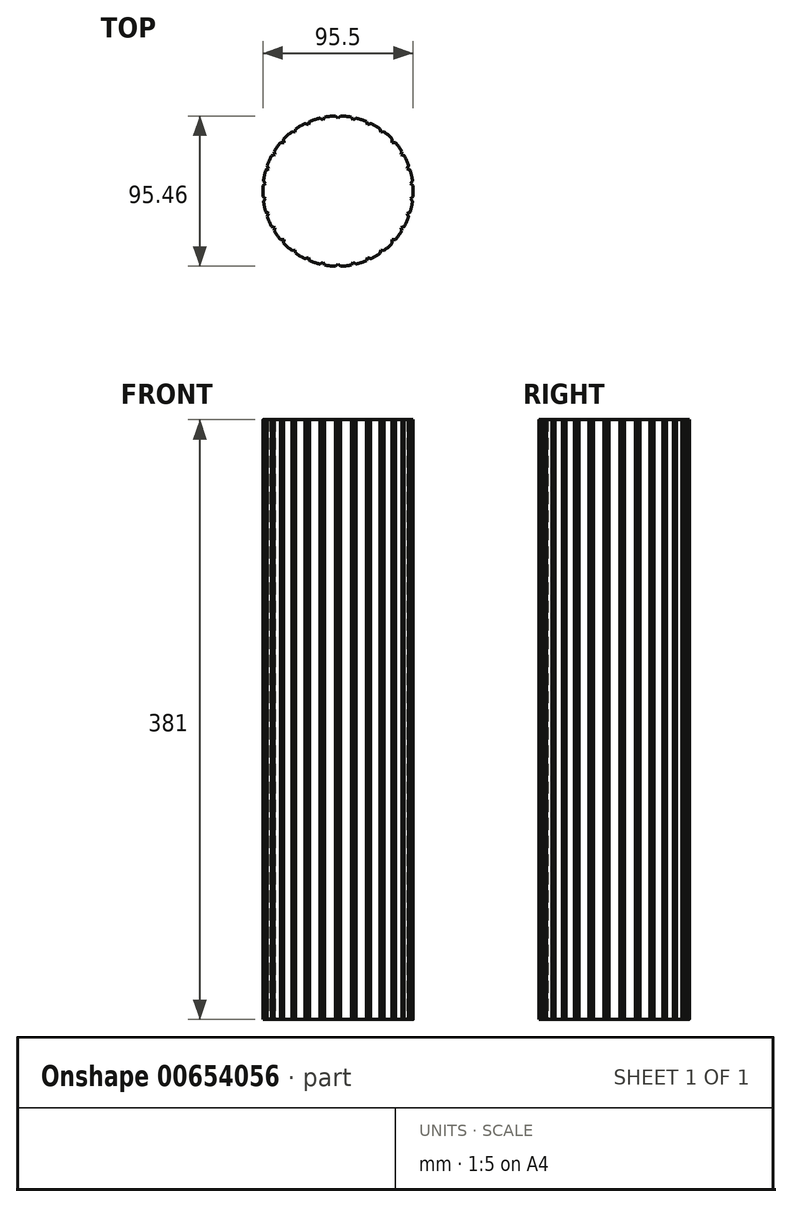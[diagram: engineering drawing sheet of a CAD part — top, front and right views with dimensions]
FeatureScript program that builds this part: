
annotation { "Feature Type Name" : "Feature", "Feature Type Description" : "" }
export const myFeature = defineFeature(function(context is Context, id is Id, definition is map)
    precondition{}
    {
        {
            var Q0;
            Q0=qCreatedBy(makeId("Top.planeOp"),FACE);
            var sketch = newSketch(context, id + "F0", { "sketchPlane" : qUnion([Q0])});
            skArc(sketch, "E0", {"start": v(1.5, -47.73) * mm, "mid": v(28.07, 38.63) * mm, "end": v(-45.86, -13.32) * mm});
            skLineSegment(sketch, "E1", {"start": v(1.5, -47.73) * mm, "end": v(0, -46.23) * mm});
            skLineSegment(sketch, "E2", {"start": v(0, -46.23) * mm, "end": v(-1.5, -47.73) * mm});
            skLineSegment(sketch, "E3.1.0", {"start": v(40.58, 25.16) * mm, "end": v(40.03, 23.11) * mm});
            skLineSegment(sketch, "E3.1.1", {"start": v(40.03, 23.11) * mm, "end": v(42.08, 22.56) * mm});
            skLineSegment(sketch, "E3.2.0", {"start": v(-42.08, 22.56) * mm, "end": v(-40.03, 23.11) * mm});
            skLineSegment(sketch, "E3.2.1", {"start": v(-40.03, 23.11) * mm, "end": v(-40.58, 25.16) * mm});
            skLineSegment(sketch, "E4.1.0", {"start": v(11.4, -46.37) * mm, "end": v(9.61, -45.22) * mm});
            skLineSegment(sketch, "E4.1.1", {"start": v(9.61, -45.22) * mm, "end": v(8.46, -47) * mm});
            skLineSegment(sketch, "E4.2.0", {"start": v(20.78, -43) * mm, "end": v(18.8, -42.23) * mm});
            skLineSegment(sketch, "E4.2.1", {"start": v(18.8, -42.23) * mm, "end": v(18.04, -44.21) * mm});
            skLineSegment(sketch, "E5.3.3.0", {"start": v(27.17, -37.4) * mm, "end": v(26.84, -39.5) * mm});
            skLineSegment(sketch, "E5.5.3.0", {"start": v(29.27, -37.73) * mm, "end": v(27.17, -37.4) * mm});
            skLineSegment(sketch, "E5.3.4.0", {"start": v(34.35, -30.93) * mm, "end": v(34.47, -33.05) * mm});
            skLineSegment(sketch, "E5.5.4.0", {"start": v(36.47, -30.82) * mm, "end": v(34.35, -30.93) * mm});
            skLineSegment(sketch, "E5.3.5.0", {"start": v(40.03, -23.11) * mm, "end": v(40.58, -25.16) * mm});
            skLineSegment(sketch, "E5.5.5.0", {"start": v(42.08, -22.56) * mm, "end": v(40.03, -23.11) * mm});
            skLineSegment(sketch, "E5.3.6.0", {"start": v(43.97, -14.29) * mm, "end": v(44.93, -16.18) * mm});
            skLineSegment(sketch, "E5.5.6.0", {"start": v(45.86, -13.32) * mm, "end": v(43.97, -14.29) * mm});
            skLineSegment(sketch, "E5.3.7.0", {"start": v(45.97, -4.83) * mm, "end": v(47.31, -6.48) * mm});
            skLineSegment(sketch, "E5.5.7.0", {"start": v(47.62, -3.5) * mm, "end": v(45.97, -4.83) * mm});
            skLineSegment(sketch, "E5.3.8.0", {"start": v(45.97, 4.83) * mm, "end": v(47.62, 3.5) * mm});
            skLineSegment(sketch, "E5.5.8.0", {"start": v(47.31, 6.48) * mm, "end": v(45.97, 4.83) * mm});
            skLineSegment(sketch, "E5.3.9.0", {"start": v(43.97, 14.29) * mm, "end": v(45.86, 13.32) * mm});
            skLineSegment(sketch, "E5.5.9.0", {"start": v(44.93, 16.18) * mm, "end": v(43.97, 14.29) * mm});
            skLineSegment(sketch, "E5.3.11.0", {"start": v(34.35, 30.93) * mm, "end": v(36.47, 30.82) * mm});
            skLineSegment(sketch, "E5.5.11.0", {"start": v(34.47, 33.05) * mm, "end": v(34.35, 30.93) * mm});
            skLineSegment(sketch, "E5.3.12.0", {"start": v(27.17, 37.4) * mm, "end": v(29.27, 37.73) * mm});
            skLineSegment(sketch, "E5.5.12.0", {"start": v(26.84, 39.5) * mm, "end": v(27.17, 37.4) * mm});
            skLineSegment(sketch, "E5.3.13.0", {"start": v(18.8, 42.23) * mm, "end": v(20.78, 43) * mm});
            skLineSegment(sketch, "E5.5.13.0", {"start": v(18.04, 44.21) * mm, "end": v(18.8, 42.23) * mm});
            skLineSegment(sketch, "E5.3.14.0", {"start": v(9.61, 45.22) * mm, "end": v(11.4, 46.37) * mm});
            skLineSegment(sketch, "E5.5.14.0", {"start": v(8.46, 47) * mm, "end": v(9.61, 45.22) * mm});
            skLineSegment(sketch, "E5.3.15.0", {"start": v(0, 46.23) * mm, "end": v(1.5, 47.73) * mm});
            skLineSegment(sketch, "E5.5.15.0", {"start": v(-1.5, 47.73) * mm, "end": v(0, 46.23) * mm});
            skLineSegment(sketch, "E5.3.16.0", {"start": v(-9.61, 45.22) * mm, "end": v(-8.46, 47) * mm});
            skLineSegment(sketch, "E5.5.16.0", {"start": v(-11.4, 46.37) * mm, "end": v(-9.61, 45.22) * mm});
            skLineSegment(sketch, "E5.3.17.0", {"start": v(-18.8, 42.23) * mm, "end": v(-18.04, 44.21) * mm});
            skLineSegment(sketch, "E5.5.17.0", {"start": v(-20.78, 43) * mm, "end": v(-18.8, 42.23) * mm});
            skLineSegment(sketch, "E5.3.18.0", {"start": v(-27.17, 37.4) * mm, "end": v(-26.84, 39.5) * mm});
            skLineSegment(sketch, "E5.5.18.0", {"start": v(-29.27, 37.73) * mm, "end": v(-27.17, 37.4) * mm});
            skLineSegment(sketch, "E5.3.19.0", {"start": v(-34.35, 30.93) * mm, "end": v(-34.47, 33.05) * mm});
            skLineSegment(sketch, "E5.5.19.0", {"start": v(-36.47, 30.82) * mm, "end": v(-34.35, 30.93) * mm});
            skLineSegment(sketch, "E5.3.21.0", {"start": v(-43.97, 14.29) * mm, "end": v(-44.93, 16.18) * mm});
            skLineSegment(sketch, "E5.5.21.0", {"start": v(-45.86, 13.32) * mm, "end": v(-43.97, 14.29) * mm});
            skLineSegment(sketch, "E5.3.22.0", {"start": v(-45.97, 4.83) * mm, "end": v(-47.31, 6.48) * mm});
            skLineSegment(sketch, "E5.5.22.0", {"start": v(-47.62, 3.5) * mm, "end": v(-45.97, 4.83) * mm});
            skLineSegment(sketch, "E5.3.23.0", {"start": v(-45.97, -4.83) * mm, "end": v(-47.62, -3.5) * mm});
            skLineSegment(sketch, "E5.5.23.0", {"start": v(-47.31, -6.48) * mm, "end": v(-45.97, -4.83) * mm});
            skLineSegment(sketch, "E5.3.24.0", {"start": v(-43.97, -14.29) * mm, "end": v(-45.86, -13.32) * mm});
            skLineSegment(sketch, "E5.5.24.0", {"start": v(-44.93, -16.18) * mm, "end": v(-43.97, -14.29) * mm});
            skLineSegment(sketch, "E5.3.25.0", {"start": v(-40.03, -23.11) * mm, "end": v(-42.08, -22.56) * mm});
            skLineSegment(sketch, "E5.5.25.0", {"start": v(-40.58, -25.16) * mm, "end": v(-40.03, -23.11) * mm});
            skLineSegment(sketch, "E5.3.26.0", {"start": v(-34.35, -30.93) * mm, "end": v(-36.47, -30.82) * mm});
            skLineSegment(sketch, "E5.5.26.0", {"start": v(-34.47, -33.05) * mm, "end": v(-34.35, -30.93) * mm});
            skLineSegment(sketch, "E5.3.27.0", {"start": v(-27.17, -37.4) * mm, "end": v(-29.27, -37.73) * mm});
            skLineSegment(sketch, "E5.5.27.0", {"start": v(-26.84, -39.5) * mm, "end": v(-27.17, -37.4) * mm});
            skLineSegment(sketch, "E5.3.28.0", {"start": v(-18.8, -42.23) * mm, "end": v(-20.78, -43) * mm});
            skLineSegment(sketch, "E5.5.28.0", {"start": v(-18.04, -44.21) * mm, "end": v(-18.8, -42.23) * mm});
            skLineSegment(sketch, "E5.3.29.0", {"start": v(-9.61, -45.22) * mm, "end": v(-11.4, -46.37) * mm});
            skLineSegment(sketch, "E5.5.29.0", {"start": v(-8.46, -47) * mm, "end": v(-9.61, -45.22) * mm});
            skArc(sketch, "E6.trimOffspring", {"start": v(-44.93, -16.18) * mm, "mid": v(-43.62, -19.42) * mm, "end": v(-42.08, -22.56) * mm});
            skArc(sketch, "E7.trimOffspring", {"start": v(-40.58, -25.16) * mm, "mid": v(-23.88, -41.35) * mm, "end": v(-1.5, -47.73) * mm});
            skSolve(sketch);
        }
        {
            var Q0;
            {var subQ24=sQuery(id+"F0.wireOp",EDGE,"E1");Q0=makeQuery(id+"F0.imprint","IMPRINT",FACE,{"disambiguationData":[TD([[makeQuery(id+"F0.imprint","IMPRINT",EDGE,{"derivedFrom":subQ24}),-1.0]])]});}
            extrude(context, id + "F1", {"entities" : qUnion([Q0]), "depth" : 381 * mm, "offsetDistance" : 25.4 * mm});
        }
    });
